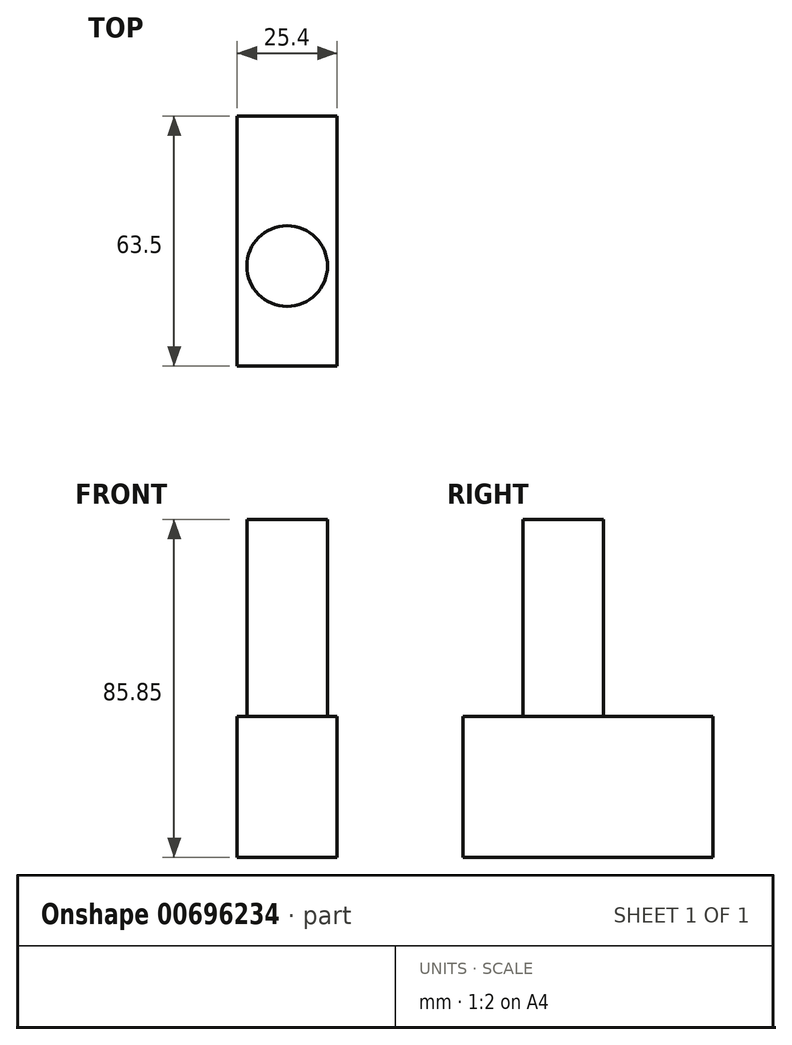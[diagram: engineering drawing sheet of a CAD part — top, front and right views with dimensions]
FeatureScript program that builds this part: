
annotation { "Feature Type Name" : "Feature", "Feature Type Description" : "" }
export const myFeature = defineFeature(function(context is Context, id is Id, definition is map)
    precondition{}
    {
        {
            var Q0;
            Q0=qCreatedBy(makeId("Front.planeOp"),FACE);
            var sketch = newSketch(context, id + "F0", { "sketchPlane" : qUnion([Q0])});
            skLineSegment(sketch, "E0.bottom", {"start": v(12.7, 12.7) * mm, "end": v(-12.7, 12.7) * mm});
            skLineSegment(sketch, "E0.top", {"start": v(12.7, -12.7) * mm, "end": v(-12.7, -12.7) * mm});
            skLineSegment(sketch, "E0.left", {"start": v(12.7, 12.7) * mm, "end": v(12.7, -12.7) * mm});
            skLineSegment(sketch, "E0.right", {"start": v(-12.7, 12.7) * mm, "end": v(-12.7, -12.7) * mm});
            skPoint(sketch, "E0.middle", {"position": v(0, 0) * mm});
            skSolve(sketch);
        }
        {
            var Q0;
            Q0 = qSketchRegion(id + "F0", true);
            extrude(context, id + "F1", {"entities" : qUnion([Q0]), "depth" : 25.4 * mm, "offsetDistance" : 25.4 * mm});
        }
        {
            var Q0;
            Q0=makeQuery(id+"F1.opExtrude","CAP_FACE",FACE,{"disambiguationData":[OSD([sQuery(id+"F0.wireOp",EDGE,"E0.bottom"),sQuery(id+"F0.wireOp",EDGE,"E0.top"),sQuery(id+"F0.wireOp",EDGE,"E0.left"),sQuery(id+"F0.wireOp",EDGE,"E0.right")])],"isStart":true});
            extrude(context, id + "F2", {"entities" : qUnion([Q0]), "operationType" : NewBodyOperationType.ADD, "depth" : 38.1 * mm, "offsetDistance" : 25.4 * mm});
        }
        {
            var Q0;
            {var subQ0=sQuery(id+"F0.wireOp",EDGE,"E0.bottom");Q0=makeQuery(id+"F2.boolean.opBoolean","MERGE",FACE,{"derivedFrom":[makeQuery(id+"F1.opExtrude","SWEPT_FACE",FACE,{"disambiguationData":[OSD([subQ0])]}),makeQuery(id+"F2.opExtrude","SWEPT_FACE",FACE,{"disambiguationData":[OSD([subQ0])]})]});}
            extrude(context, id + "F3", {"entities" : qUnion([Q0]), "operationType" : NewBodyOperationType.ADD, "depth" : 10.4 * mm, "offsetDistance" : 25.4 * mm});
        }
        {
            var Q0;
            Q0=qCreatedBy(makeId("Top.planeOp"),FACE);
            var sketch = newSketch(context, id + "F4", { "sketchPlane" : qUnion([Q0])});
            skCircle(sketch, "E1", {"center": v(0, 0) * mm, "radius": 10.25 * mm});
            skSolve(sketch);
        }
        {
            var Q0;
            Q0 = qSketchRegion(id + "F4", true);
            extrude(context, id + "F5", {"entities" : qUnion([Q0]), "operationType" : NewBodyOperationType.ADD, "depth" : 73.15 * mm, "offsetDistance" : 25.4 * mm});
        }
        {
            var Q0;
            Q0=sQuery(id+"F4.wireOp",EDGE,"E1");
            extrude(context, id + "F6", {"bodyType" : ToolBodyType.SURFACE, "surfaceEntities" : qUnion([Q0]), "oppositeDirection" : true, "depth" : 67.3 * mm, "offsetDistance" : 25.4 * mm});
        }
    });
